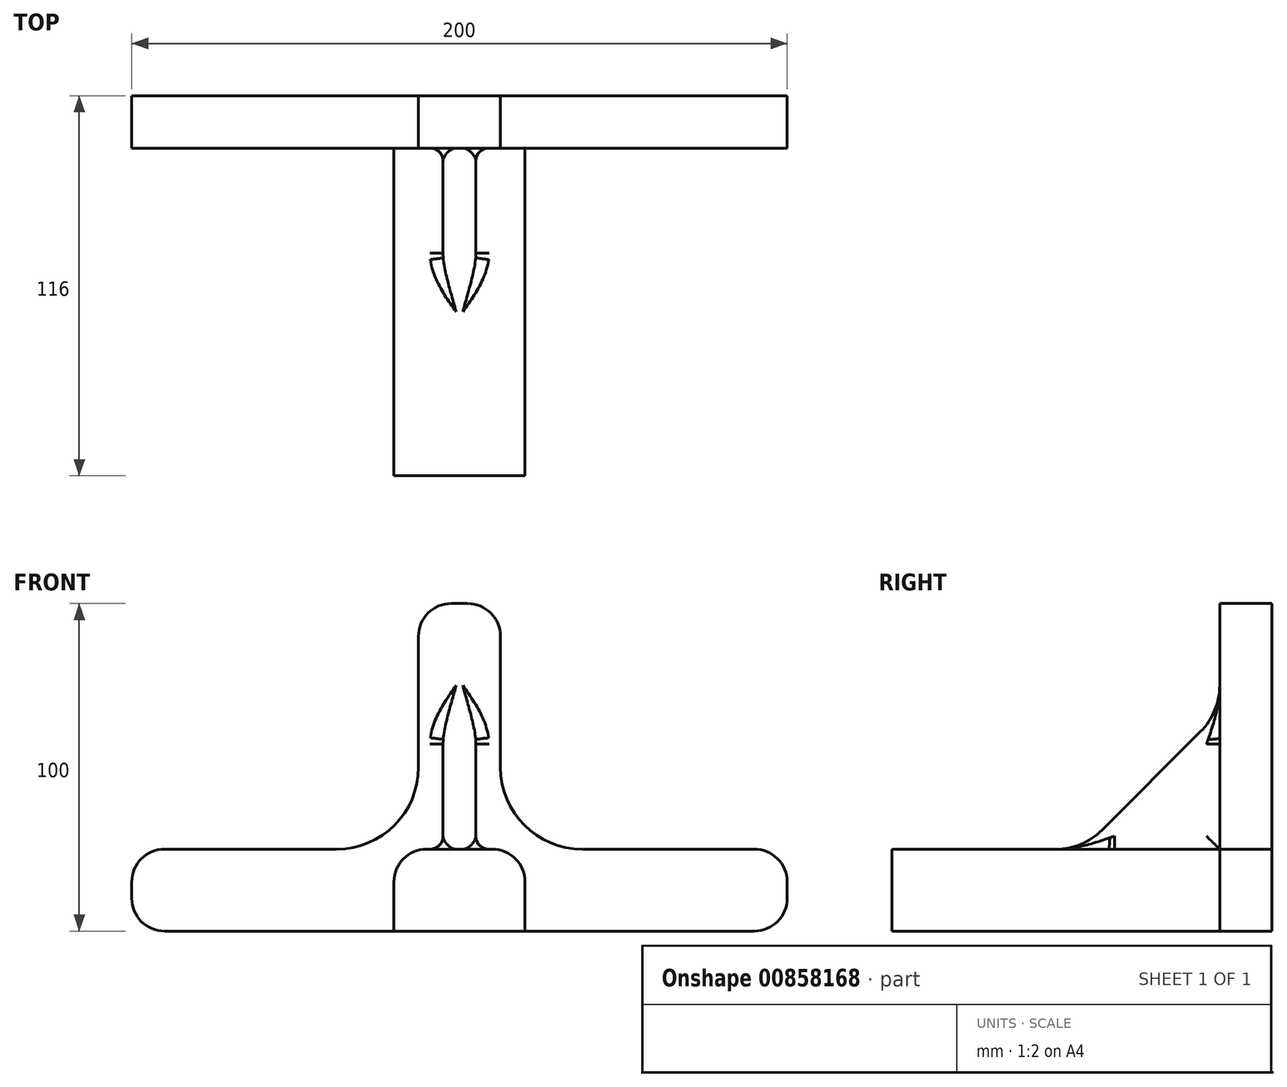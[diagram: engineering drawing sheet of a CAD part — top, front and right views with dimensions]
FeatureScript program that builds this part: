
annotation { "Feature Type Name" : "Feature", "Feature Type Description" : "" }
export const myFeature = defineFeature(function(context is Context, id is Id, definition is map)
    precondition{}
    {
        {
            var Q0;
            Q0=qCreatedBy(makeId("Front.planeOp"),FACE);
            var sketch = newSketch(context, id + "F0", { "sketchPlane" : qUnion([Q0])});
            skLineSegment(sketch, "E0.bottom", {"start": v(-100, 25) * mm, "end": v(-12.5, 25) * mm});
            skLineSegment(sketch, "E0.top", {"start": v(-100, 0) * mm, "end": v(100, 0) * mm});
            skLineSegment(sketch, "E0.left", {"start": v(-100, 25) * mm, "end": v(-100, 0) * mm});
            skLineSegment(sketch, "E0.right", {"start": v(100, 25) * mm, "end": v(100, 0) * mm});
            skLineSegment(sketch, "E1.bottom", {"start": v(-12.5, 100) * mm, "end": v(12.5, 100) * mm});
            skLineSegment(sketch, "E1.left", {"start": v(-12.5, 100) * mm, "end": v(-12.5, 25) * mm});
            skLineSegment(sketch, "E1.right", {"start": v(12.5, 100) * mm, "end": v(12.5, 25) * mm});
            skLineSegment(sketch, "E2.trimOffspring", {"start": v(12.5, 25) * mm, "end": v(100, 25) * mm});
            skLineSegment(sketch, "E3", {"start": v(0, 100) * mm, "end": v(0, 0) * mm, "construction": true});
            skSolve(sketch);
        }
        {
            var Q0;
            Q0 = qSketchRegion(id + "F0", true);
            extrude(context, id + "F1", {"entities" : qUnion([Q0]), "depth" : 16 * mm, "offsetDistance" : 25 * mm});
        }
        {
            var Q0;
            Q0=makeQuery(id+"F1.opExtrude","SWEPT_EDGE",EDGE,{"disambiguationData":[OSD([sQuery(id+"F0.wireOp",EDGE,"E0.bottom"),sQuery(id+"F0.wireOp",EDGE,"E1.left")])]});
            var Q1;
            Q1=makeQuery(id+"F1.opExtrude","SWEPT_EDGE",EDGE,{"disambiguationData":[OSD([sQuery(id+"F0.wireOp",EDGE,"E1.right"),sQuery(id+"F0.wireOp",EDGE,"E2.trimOffspring")])]});
            fillet(context, id + "F2", {"entities" : qUnion([Q0, Q1]), "radius" : 25 * mm, "tangentPropagation" : true, "allowEdgeOverflow" : false});
        }
        {
            var Q0;
            Q0=makeQuery(id+"F1.opExtrude","SWEPT_EDGE",EDGE,{"disambiguationData":[OSD([sQuery(id+"F0.wireOp",EDGE,"E1.bottom"),sQuery(id+"F0.wireOp",EDGE,"E1.left")])]});
            var Q1;
            Q1=makeQuery(id+"F1.opExtrude","SWEPT_EDGE",EDGE,{"disambiguationData":[OSD([sQuery(id+"F0.wireOp",EDGE,"E1.bottom"),sQuery(id+"F0.wireOp",EDGE,"E1.right")])]});
            var Q2;
            Q2=makeQuery(id+"F1.opExtrude","SWEPT_EDGE",EDGE,{"disambiguationData":[OSD([sQuery(id+"F0.wireOp",EDGE,"E0.right"),sQuery(id+"F0.wireOp",EDGE,"E2.trimOffspring")])]});
            var Q3;
            Q3=makeQuery(id+"F1.opExtrude","SWEPT_EDGE",EDGE,{"disambiguationData":[OSD([sQuery(id+"F0.wireOp",EDGE,"E0.top"),sQuery(id+"F0.wireOp",EDGE,"E0.right")])]});
            var Q4;
            Q4=makeQuery(id+"F1.opExtrude","SWEPT_EDGE",EDGE,{"disambiguationData":[OSD([sQuery(id+"F0.wireOp",EDGE,"E0.bottom"),sQuery(id+"F0.wireOp",EDGE,"E0.left")])]});
            var Q5;
            Q5=makeQuery(id+"F1.opExtrude","SWEPT_EDGE",EDGE,{"disambiguationData":[OSD([sQuery(id+"F0.wireOp",EDGE,"E0.top"),sQuery(id+"F0.wireOp",EDGE,"E0.left")])]});
            fillet(context, id + "F3", {"entities" : qUnion([Q0, Q1, Q2, Q3, Q4, Q5]), "radius" : 10 * mm, "tangentPropagation" : true, "allowEdgeOverflow" : false});
        }
        {
            var Q0;
            Q0=makeQuery(id+"F1.opExtrude","CAP_FACE",FACE,{"disambiguationData":[OSD([sQuery(id+"F0.wireOp",EDGE,"E0.bottom"),sQuery(id+"F0.wireOp",EDGE,"E0.top"),sQuery(id+"F0.wireOp",EDGE,"E0.left"),sQuery(id+"F0.wireOp",EDGE,"E0.right"),sQuery(id+"F0.wireOp",EDGE,"E1.bottom"),sQuery(id+"F0.wireOp",EDGE,"E1.left"),sQuery(id+"F0.wireOp",EDGE,"E1.right"),sQuery(id+"F0.wireOp",EDGE,"E2.trimOffspring")])],"isStart":false});
            var sketch = newSketch(context, id + "F4", { "sketchPlane" : qUnion([Q0])});
            skLineSegment(sketch, "E4.bottom", {"start": v(-20, 0) * mm, "end": v(20, 0) * mm});
            skLineSegment(sketch, "E4.top", {"start": v(-10, 25) * mm, "end": v(10, 25) * mm});
            skLineSegment(sketch, "E4.left", {"start": v(-20, 0) * mm, "end": v(-20, 15) * mm});
            skLineSegment(sketch, "E4.right", {"start": v(20, 0) * mm, "end": v(20, 15) * mm});
            skLineSegment(sketch, "E5", {"start": v(0, 100) * mm, "end": v(0, 0) * mm, "construction": true});
            skPoint(sketch, "E6.visualSharp", {"position": v(-20, 25) * mm});
            skArc(sketch, "E6.filletArc", {"start": v(-10, 25) * mm, "mid": v(-17.07, 22.07) * mm, "end": v(-20, 15) * mm});
            skPoint(sketch, "E7.visualSharp", {"position": v(20, 25) * mm});
            skArc(sketch, "E7.filletArc", {"start": v(20, 15) * mm, "mid": v(17.07, 22.07) * mm, "end": v(10, 25) * mm});
            skSolve(sketch);
        }
        {
            var Q0;
            Q0 = qSketchRegion(id + "F4", true);
            extrude(context, id + "F5", {"entities" : qUnion([Q0]), "operationType" : NewBodyOperationType.ADD, "depth" : 100 * mm, "offsetDistance" : 25 * mm});
        }
        {
            var Q0;
            Q0=qCreatedBy(makeId("Right.planeOp"),FACE);
            var sketch = newSketch(context, id + "F6", { "sketchPlane" : qUnion([Q0])});
            skLineSegment(sketch, "E8", {"start": v(-21.86, 60.86) * mm, "end": v(-51.86, 30.86) * mm});
            skArc(sketch, "E9", {"start": v(-66, 25) * mm, "mid": v(-58.35, 26.52) * mm, "end": v(-51.86, 30.86) * mm});
            skLineSegment(sketch, "E10", {"start": v(-16, 25) * mm, "end": v(-66, 25) * mm});
            skArc(sketch, "E11", {"start": v(-21.86, 60.86) * mm, "mid": v(-17.52, 67.35) * mm, "end": v(-16, 75) * mm});
            skLineSegment(sketch, "E12", {"start": v(-16, 25) * mm, "end": v(-16, 75) * mm});
            skSolve(sketch);
        }
        {
            var Q0;
            Q0 = qSketchRegion(id + "F6", true);
            extrude(context, id + "F7", {"entities" : qUnion([Q0]), "operationType" : NewBodyOperationType.ADD, "endBound" : BoundingType.SYMMETRIC, "depth" : 10 * mm, "offsetDistance" : 25 * mm});
        }
        {
            var Q0;
            Q0=makeQuery(id+"F7.opExtrude","CAP_EDGE",EDGE,{"disambiguationData":[OSD([sQuery(id+"F6.wireOp",EDGE,"E12")])],"isStart":true});
            var Q1;
            Q1=makeQuery(id+"F7.opExtrude","CAP_FACE",FACE,{"disambiguationData":[OSD([sQuery(id+"F6.wireOp",EDGE,"E8"),sQuery(id+"F6.wireOp",EDGE,"E9"),sQuery(id+"F6.wireOp",EDGE,"E10"),sQuery(id+"F6.wireOp",EDGE,"E11"),sQuery(id+"F6.wireOp",EDGE,"E12")])],"isStart":true});
            var Q2;
            Q2=makeQuery(id+"F7.opExtrude","CAP_FACE",FACE,{"disambiguationData":[OSD([sQuery(id+"F6.wireOp",EDGE,"E8"),sQuery(id+"F6.wireOp",EDGE,"E9"),sQuery(id+"F6.wireOp",EDGE,"E10"),sQuery(id+"F6.wireOp",EDGE,"E11"),sQuery(id+"F6.wireOp",EDGE,"E12")])],"isStart":false});
            fillet(context, id + "F8", {"entities" : qUnion([Q0, Q1, Q2]), "radius" : 4 * mm, "tangentPropagation" : true, "allowEdgeOverflow" : false});
        }
    });
